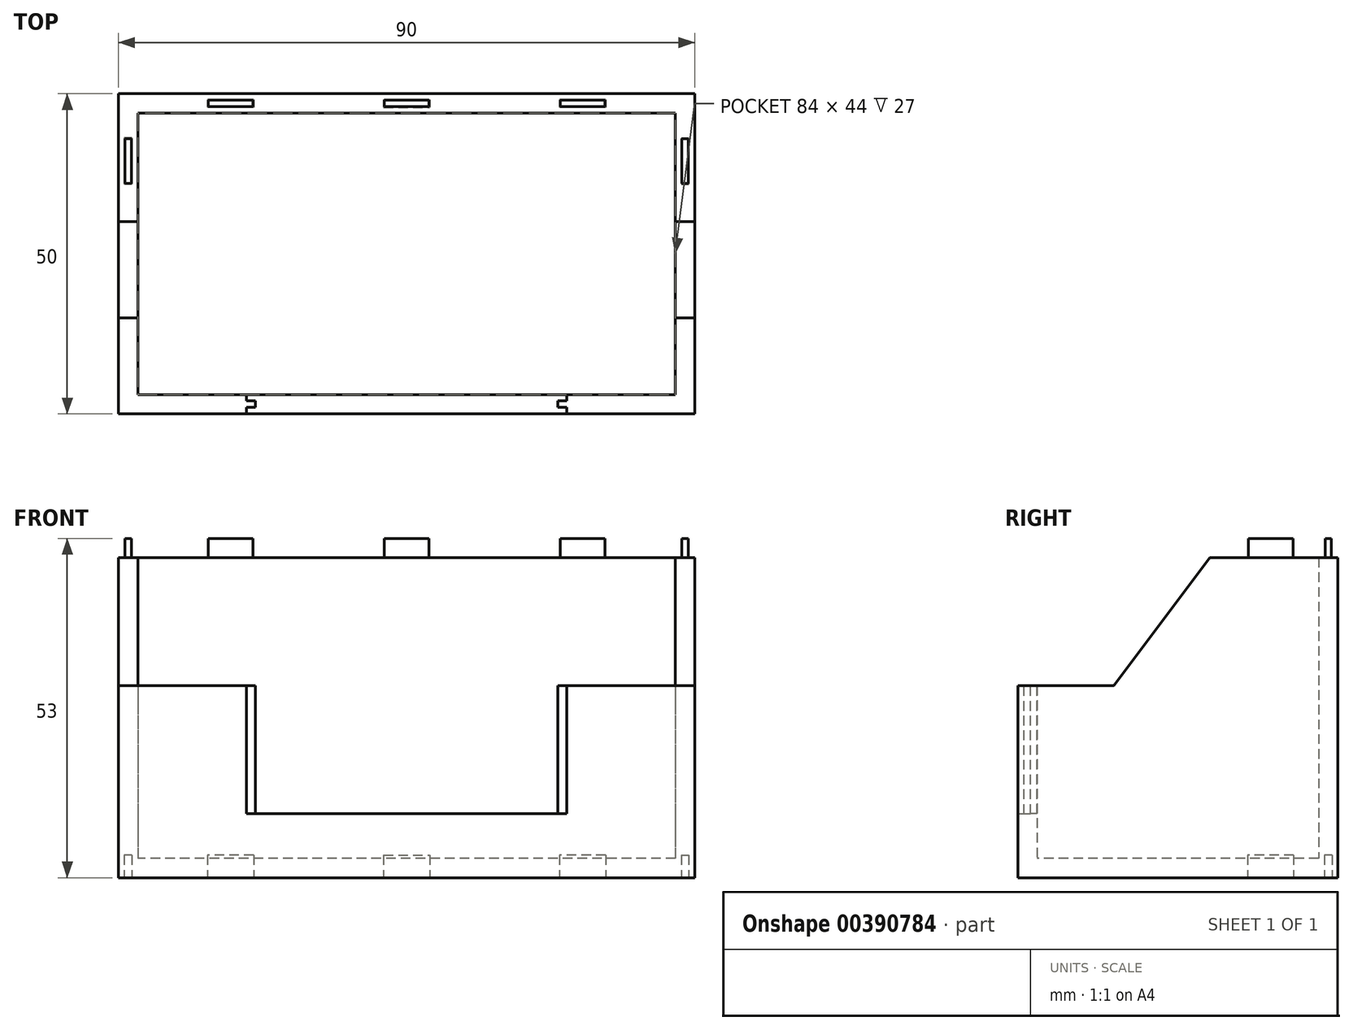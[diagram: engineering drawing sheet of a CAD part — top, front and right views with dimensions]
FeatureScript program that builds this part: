
annotation { "Feature Type Name" : "Feature", "Feature Type Description" : "" }
export const myFeature = defineFeature(function(context is Context, id is Id, definition is map)
    precondition{}
    {
        {
            var Q0;
            Q0=qCreatedBy(makeId("Top.planeOp"),FACE);
            var sketch = newSketch(context, id + "F0", { "sketchPlane" : qUnion([Q0])});
            skLineSegment(sketch, "E0.bottom", {"start": v(45, 25) * mm, "end": v(-45, 25) * mm});
            skLineSegment(sketch, "E0.top", {"start": v(45, -25) * mm, "end": v(-45, -25) * mm});
            skLineSegment(sketch, "E0.left", {"start": v(45, 25) * mm, "end": v(45, -25) * mm});
            skLineSegment(sketch, "E0.right", {"start": v(-45, 25) * mm, "end": v(-45, -25) * mm});
            skPoint(sketch, "E0.middle", {"position": v(0, 0) * mm});
            skSolve(sketch);
        }
        {
            var Q0;
            Q0 = qSketchRegion(id + "F0", true);
            extrude(context, id + "F1", {"entities" : qUnion([Q0]), "depth" : 50 * mm});
        }
        {
            var Q0;
            Q0=makeQuery(id+"F1.opExtrude","CAP_FACE",FACE,{"disambiguationData":[OSD([sQuery(id+"F0.wireOp",EDGE,"E0.bottom"),sQuery(id+"F0.wireOp",EDGE,"E0.top"),sQuery(id+"F0.wireOp",EDGE,"E0.left"),sQuery(id+"F0.wireOp",EDGE,"E0.right")])],"isStart":false});
            shell(context, id + "F2", {"entities" : qUnion([Q0]), "thickness" : 3 * mm});
        }
        {
            var Q0;
            Q0=makeQuery(id+"F1.opExtrude","SWEPT_FACE",FACE,{"disambiguationData":[OSD([sQuery(id+"F0.wireOp",EDGE,"E0.right")])]});
            var sketch = newSketch(context, id + "F3", { "sketchPlane" : qUnion([Q0])});
            skLineSegment(sketch, "E1", {"start": v(25, 50) * mm, "end": v(25, 30) * mm});
            skLineSegment(sketch, "E2", {"start": v(25, 30) * mm, "end": v(10, 30) * mm});
            skLineSegment(sketch, "E3", {"start": v(10, 30) * mm, "end": v(-5, 50) * mm});
            skLineSegment(sketch, "E4", {"start": v(-5, 50) * mm, "end": v(25, 50) * mm});
            skSolve(sketch);
        }
        {
            var Q0;
            Q0 = qSketchRegion(id + "F3", true);
            extrude(context, id + "F4", {"entities" : qUnion([Q0]), "operationType" : NewBodyOperationType.REMOVE, "endBound" : BoundingType.THROUGH_ALL, "oppositeDirection" : true, "depth" : 25 * mm});
        }
        {
            var Q0;
            Q0=makeQuery(id+"F4.boolean.opBoolean","COPY",FACE,{"derivedFrom":makeQuery(id+"F4.opExtrude","SWEPT_FACE",FACE,{"disambiguationData":[OSD([sQuery(id+"F3.wireOp",EDGE,"E2")])]})});
            var sketch = newSketch(context, id + "F5", { "sketchPlane" : qUnion([Q0])});
            skLineSegment(sketch, "E5", {"start": v(-25, -22) * mm, "end": v(25, -22) * mm});
            skLineSegment(sketch, "E6", {"start": v(25, -22) * mm, "end": v(25, -23) * mm});
            skLineSegment(sketch, "E7", {"start": v(25, -23) * mm, "end": v(23.6, -23) * mm});
            skLineSegment(sketch, "E8", {"start": v(23.6, -23) * mm, "end": v(23.6, -24) * mm});
            skLineSegment(sketch, "E9", {"start": v(23.6, -24) * mm, "end": v(25, -24) * mm});
            skLineSegment(sketch, "E10", {"start": v(25, -24) * mm, "end": v(25, -25) * mm});
            skLineSegment(sketch, "E11", {"start": v(25, -25) * mm, "end": v(-25, -25) * mm});
            skLineSegment(sketch, "E12", {"start": v(-25, -25) * mm, "end": v(-25, -24) * mm});
            skLineSegment(sketch, "E13", {"start": v(-25, -24) * mm, "end": v(-23.6, -24) * mm});
            skLineSegment(sketch, "E14", {"start": v(-23.6, -24) * mm, "end": v(-23.6, -23) * mm});
            skLineSegment(sketch, "E15", {"start": v(-23.6, -23) * mm, "end": v(-25, -23) * mm});
            skLineSegment(sketch, "E16", {"start": v(-25, -23) * mm, "end": v(-25, -22) * mm});
            skSolve(sketch);
        }
        {
            var Q0;
            Q0 = qSketchRegion(id + "F5", true);
            extrude(context, id + "F6", {"entities" : qUnion([Q0]), "operationType" : NewBodyOperationType.REMOVE, "oppositeDirection" : true, "depth" : 20 * mm});
        }
        {
            var Q0;
            Q0=makeQuery(id+"F1.opExtrude","CAP_FACE",FACE,{"disambiguationData":[OSD([sQuery(id+"F0.wireOp",EDGE,"E0.bottom"),sQuery(id+"F0.wireOp",EDGE,"E0.top"),sQuery(id+"F0.wireOp",EDGE,"E0.left"),sQuery(id+"F0.wireOp",EDGE,"E0.right")])],"isStart":false});
            var sketch = newSketch(context, id + "F7", { "sketchPlane" : qUnion([Q0])});
            skLineSegment(sketch, "E17.bottom", {"start": v(-31, 24) * mm, "end": v(-24, 24) * mm});
            skLineSegment(sketch, "E17.top", {"start": v(-31, 23) * mm, "end": v(-24, 23) * mm});
            skLineSegment(sketch, "E17.left", {"start": v(-31, 24) * mm, "end": v(-31, 23) * mm});
            skLineSegment(sketch, "E17.right", {"start": v(-24, 24) * mm, "end": v(-24, 23) * mm});
            skLineSegment(sketch, "E18.bottom", {"start": v(-44, 11) * mm, "end": v(-43, 11) * mm});
            skLineSegment(sketch, "E18.top", {"start": v(-44, 18) * mm, "end": v(-43, 18) * mm});
            skLineSegment(sketch, "E18.left", {"start": v(-44, 11) * mm, "end": v(-44, 18) * mm});
            skLineSegment(sketch, "E18.right", {"start": v(-43, 11) * mm, "end": v(-43, 18) * mm});
            skLineSegment(sketch, "E19.bottom", {"start": v(24, 24) * mm, "end": v(31, 24) * mm});
            skLineSegment(sketch, "E19.top", {"start": v(24, 23) * mm, "end": v(31, 23) * mm});
            skLineSegment(sketch, "E19.left", {"start": v(24, 24) * mm, "end": v(24, 23) * mm});
            skLineSegment(sketch, "E19.right", {"start": v(31, 24) * mm, "end": v(31, 23) * mm});
            skLineSegment(sketch, "E20.bottom", {"start": v(43, 11) * mm, "end": v(44, 11) * mm});
            skLineSegment(sketch, "E20.top", {"start": v(43, 18) * mm, "end": v(44, 18) * mm});
            skLineSegment(sketch, "E20.left", {"start": v(43, 11) * mm, "end": v(43, 18) * mm});
            skLineSegment(sketch, "E20.right", {"start": v(44, 11) * mm, "end": v(44, 18) * mm});
            skLineSegment(sketch, "E21.bottom", {"start": v(-3.5, 24) * mm, "end": v(3.5, 24) * mm});
            skLineSegment(sketch, "E21.top", {"start": v(-3.5, 23) * mm, "end": v(3.5, 23) * mm});
            skLineSegment(sketch, "E21.left", {"start": v(-3.5, 24) * mm, "end": v(-3.5, 23) * mm});
            skLineSegment(sketch, "E21.right", {"start": v(3.5, 24) * mm, "end": v(3.5, 23) * mm});
            skSolve(sketch);
        }
        {
            var Q0;
            Q0 = qSketchRegion(id + "F7", true);
            extrude(context, id + "F8", {"entities" : qUnion([Q0]), "operationType" : NewBodyOperationType.ADD, "depth" : 3 * mm});
        }
        {
            var Q0;
            Q0=makeQuery(id+"F1.opExtrude","CAP_FACE",FACE,{"disambiguationData":[OSD([sQuery(id+"F0.wireOp",EDGE,"E0.bottom"),sQuery(id+"F0.wireOp",EDGE,"E0.top"),sQuery(id+"F0.wireOp",EDGE,"E0.left"),sQuery(id+"F0.wireOp",EDGE,"E0.right")])],"isStart":true});
            var sketch = newSketch(context, id + "F9", { "sketchPlane" : qUnion([Q0])});
            skLineSegment(sketch, "E22.bottom", {"start": v(-3.6, -24.1) * mm, "end": v(3.6, -24.1) * mm});
            skLineSegment(sketch, "E22.top", {"start": v(-3.6, -22.9) * mm, "end": v(3.6, -22.9) * mm});
            skLineSegment(sketch, "E22.left", {"start": v(-3.6, -24.1) * mm, "end": v(-3.6, -22.9) * mm});
            skLineSegment(sketch, "E22.right", {"start": v(3.6, -24.1) * mm, "end": v(3.6, -22.9) * mm});
            skLineSegment(sketch, "E23.bottom", {"start": v(31.1, -24.1) * mm, "end": v(23.9, -24.1) * mm});
            skLineSegment(sketch, "E23.top", {"start": v(31.1, -22.9) * mm, "end": v(23.9, -22.9) * mm});
            skLineSegment(sketch, "E23.left", {"start": v(31.1, -24.1) * mm, "end": v(31.1, -22.9) * mm});
            skLineSegment(sketch, "E23.right", {"start": v(23.9, -24.1) * mm, "end": v(23.9, -22.9) * mm});
            skLineSegment(sketch, "E24.bottom", {"start": v(-23.9, -24.1) * mm, "end": v(-31.1, -24.1) * mm});
            skLineSegment(sketch, "E24.top", {"start": v(-23.9, -22.9) * mm, "end": v(-31.1, -22.9) * mm});
            skLineSegment(sketch, "E24.left", {"start": v(-23.9, -24.1) * mm, "end": v(-23.9, -22.9) * mm});
            skLineSegment(sketch, "E24.right", {"start": v(-31.1, -24.1) * mm, "end": v(-31.1, -22.9) * mm});
            skLineSegment(sketch, "E25.bottom", {"start": v(42.9, -18.1) * mm, "end": v(44.1, -18.1) * mm});
            skLineSegment(sketch, "E25.top", {"start": v(42.9, -10.9) * mm, "end": v(44.1, -10.9) * mm});
            skLineSegment(sketch, "E25.left", {"start": v(42.9, -18.1) * mm, "end": v(42.9, -10.9) * mm});
            skLineSegment(sketch, "E25.right", {"start": v(44.1, -18.1) * mm, "end": v(44.1, -10.9) * mm});
            skLineSegment(sketch, "E26.bottom", {"start": v(-42.9, -18.1) * mm, "end": v(-44.1, -18.1) * mm});
            skLineSegment(sketch, "E26.top", {"start": v(-42.9, -10.9) * mm, "end": v(-44.1, -10.9) * mm});
            skLineSegment(sketch, "E26.left", {"start": v(-42.9, -18.1) * mm, "end": v(-42.9, -10.9) * mm});
            skLineSegment(sketch, "E26.right", {"start": v(-44.1, -18.1) * mm, "end": v(-44.1, -10.9) * mm});
            skSolve(sketch);
        }
        {
            var Q0;
            Q0 = qSketchRegion(id + "F9", true);
            extrude(context, id + "F10", {"entities" : qUnion([Q0]), "operationType" : NewBodyOperationType.REMOVE, "oppositeDirection" : true, "depth" : 3.5 * mm});
        }
    });
